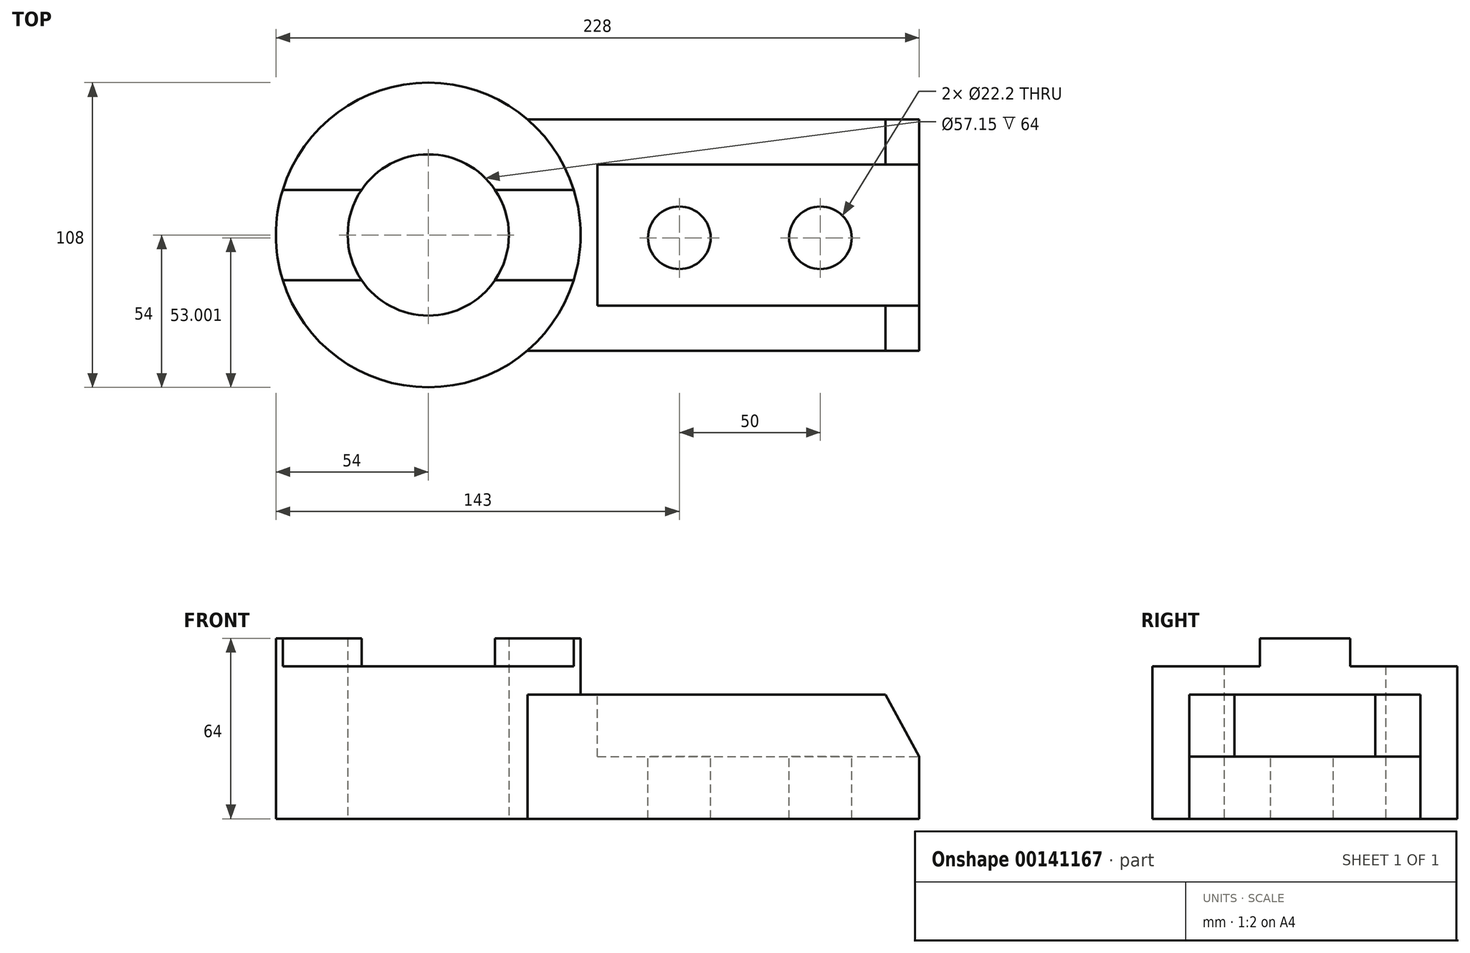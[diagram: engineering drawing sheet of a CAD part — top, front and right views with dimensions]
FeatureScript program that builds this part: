
annotation { "Feature Type Name" : "Feature", "Feature Type Description" : "" }
export const myFeature = defineFeature(function(context is Context, id is Id, definition is map)
    precondition{}
    {
        {
            var Q0;
            Q0=qCreatedBy(makeId("Top.planeOp"),FACE);
            var sketch = newSketch(context, id + "F0", { "sketchPlane" : qUnion([Q0])});
            skLineSegment(sketch, "E0", {"start": v(0, 0) * mm, "end": v(0, 82) * mm});
            skLineSegment(sketch, "E1", {"start": v(0, 82) * mm, "end": v(139.29, 82) * mm});
            skLineSegment(sketch, "E2", {"start": v(139.29, 82) * mm, "end": v(139.29, 0) * mm});
            skLineSegment(sketch, "E3", {"start": v(139.29, 0) * mm, "end": v(0, 0) * mm});
            skCircle(sketch, "E4", {"center": v(-34.7, 41) * mm, "radius": 54 * mm});
            skCircle(sketch, "E5", {"center": v(-34.7, 41) * mm, "radius": 28.57 * mm});
            skSolve(sketch);
        }
        {
            var Q0;
            {var subQ5=sQuery(id+"F0.wireOp",EDGE,"E0");Q0=makeQuery(id+"F0.imprint","IMPRINT",FACE,{"disambiguationData":[TD([[makeQuery(id+"F0.imprint","IMPRINT",EDGE,{"derivedFrom":subQ5}),1.0]])]});}
            var Q1;
            {var subQ0=sQuery(id+"F0.wireOp",EDGE,"E0");Q1=makeQuery(id+"F0.imprint","IMPRINT",FACE,{"disambiguationData":[TD([[makeQuery(id+"F0.imprint","IMPRINT",EDGE,{"derivedFrom":subQ0}),-1.0]])]});}
            extrude(context, id + "F1", {"entities" : qUnion([Q0, Q1]), "depth" : 64 * mm});
        }
        {
            var Q0;
            {var subQ0=sQuery(id+"F0.wireOp",EDGE,"E2");Q0=makeQuery(id+"F0.imprint","IMPRINT",FACE,{"disambiguationData":[TD([[makeQuery(id+"F0.imprint","IMPRINT",EDGE,{"derivedFrom":subQ0}),-1.0]])]});}
            extrude(context, id + "F2", {"entities" : qUnion([Q0]), "operationType" : NewBodyOperationType.ADD, "depth" : 44 * mm});
        }
        {
            var Q0;
            Q0=makeQuery(id+"F1.opExtrude","CAP_FACE",FACE,{"disambiguationData":[OSD([sQuery(id+"F0.wireOp",EDGE,"E4"),sQuery(id+"F0.wireOp",EDGE,"E5")])],"isStart":false});
            var sketch = newSketch(context, id + "F3", { "sketchPlane" : qUnion([Q0])});
            skLineSegment(sketch, "E6", {"start": v(16.87, -24.65) * mm, "end": v(-86.29, -24.65) * mm});
            skLineSegment(sketch, "E7", {"start": v(-86.29, -24.65) * mm, "end": v(-86.29, 25) * mm});
            skLineSegment(sketch, "E8", {"start": v(16.87, 25) * mm, "end": v(16.87, -24.65) * mm});
            skLineSegment(sketch, "E9", {"start": v(-86.29, 57) * mm, "end": v(-86.29, 100.7) * mm});
            skLineSegment(sketch, "E10", {"start": v(-86.29, 100.7) * mm, "end": v(16.87, 100.7) * mm});
            skLineSegment(sketch, "E11", {"start": v(16.87, 100.7) * mm, "end": v(16.87, 57) * mm});
            skLineSegment(sketch, "E12", {"start": v(-86.29, 57) * mm, "end": v(16.87, 57) * mm});
            skLineSegment(sketch, "E13", {"start": v(16.87, 25) * mm, "end": v(-86.29, 25) * mm});
            skSolve(sketch);
        }
        {
            var Q0;
            Q0 = qSketchRegion(id + "F3", true);
            extrude(context, id + "F4", {"entities" : qUnion([Q0]), "operationType" : NewBodyOperationType.REMOVE, "oppositeDirection" : true, "depth" : 10 * mm});
        }
        {
            var Q0;
            Q0=makeQuery(id+"F2.opExtrude","CAP_FACE",FACE,{"disambiguationData":[OSD([sQuery(id+"F0.wireOp",EDGE,"E1"),sQuery(id+"F0.wireOp",EDGE,"E2"),sQuery(id+"F0.wireOp",EDGE,"E3"),sQuery(id+"F0.wireOp",EDGE,"E4")])],"isStart":false});
            var sketch = newSketch(context, id + "F5", { "sketchPlane" : qUnion([Q0])});
            skLineSegment(sketch, "E14", {"start": v(25.29, 66) * mm, "end": v(139.29, 66) * mm});
            skLineSegment(sketch, "E15", {"start": v(139.29, 66) * mm, "end": v(139.29, 16) * mm});
            skLineSegment(sketch, "E16", {"start": v(139.29, 16) * mm, "end": v(25.29, 16) * mm});
            skLineSegment(sketch, "E17", {"start": v(25.29, 16) * mm, "end": v(25.29, 66) * mm});
            skSolve(sketch);
        }
        {
            var Q0;
            Q0 = qSketchRegion(id + "F5", true);
            extrude(context, id + "F6", {"entities" : qUnion([Q0]), "operationType" : NewBodyOperationType.REMOVE, "oppositeDirection" : true, "depth" : 22 * mm});
        }
        {
            var Q0;
            Q0=makeQuery(id+"F2.opExtrude","SWEPT_FACE",FACE,{"disambiguationData":[OSD([sQuery(id+"F0.wireOp",EDGE,"E3")])]});
            var sketch = newSketch(context, id + "F7", { "sketchPlane" : qUnion([Q0])});
            skLineSegment(sketch, "E18", {"start": v(139.29, 44) * mm, "end": v(139.29, 22) * mm});
            skLineSegment(sketch, "E19", {"start": v(139.29, 44) * mm, "end": v(127.29, 44) * mm});
            skLineSegment(sketch, "E20", {"start": v(127.29, 44) * mm, "end": v(139.29, 22) * mm});
            skSolve(sketch);
        }
        {
            var Q0;
            Q0 = qSketchRegion(id + "F7", true);
            extrude(context, id + "F8", {"entities" : qUnion([Q0]), "operationType" : NewBodyOperationType.REMOVE, "endBound" : BoundingType.THROUGH_ALL, "oppositeDirection" : true, "depth" : 25 * mm});
        }
        {
            var Q0;
            Q0=makeQuery(id+"F6.boolean.opBoolean","COPY",FACE,{"derivedFrom":makeQuery(id+"F6.opExtrude","CAP_FACE",FACE,{"disambiguationData":[OSD([sQuery(id+"F5.wireOp",EDGE,"E14"),sQuery(id+"F5.wireOp",EDGE,"E15"),sQuery(id+"F5.wireOp",EDGE,"E16"),sQuery(id+"F5.wireOp",EDGE,"E17")])],"isStart":false})});
            var sketch = newSketch(context, id + "F9", { "sketchPlane" : qUnion([Q0])});
            skCircle(sketch, "E21", {"center": v(54.29, 40) * mm, "radius": 11.1 * mm});
            skCircle(sketch, "E22", {"center": v(104.29, 40) * mm, "radius": 11.1 * mm});
            skSolve(sketch);
        }
        {
            var Q0;
            Q0 = qSketchRegion(id + "F9", true);
            extrude(context, id + "F10", {"entities" : qUnion([Q0]), "operationType" : NewBodyOperationType.REMOVE, "endBound" : BoundingType.THROUGH_ALL, "oppositeDirection" : true, "depth" : 25 * mm});
        }
    });
